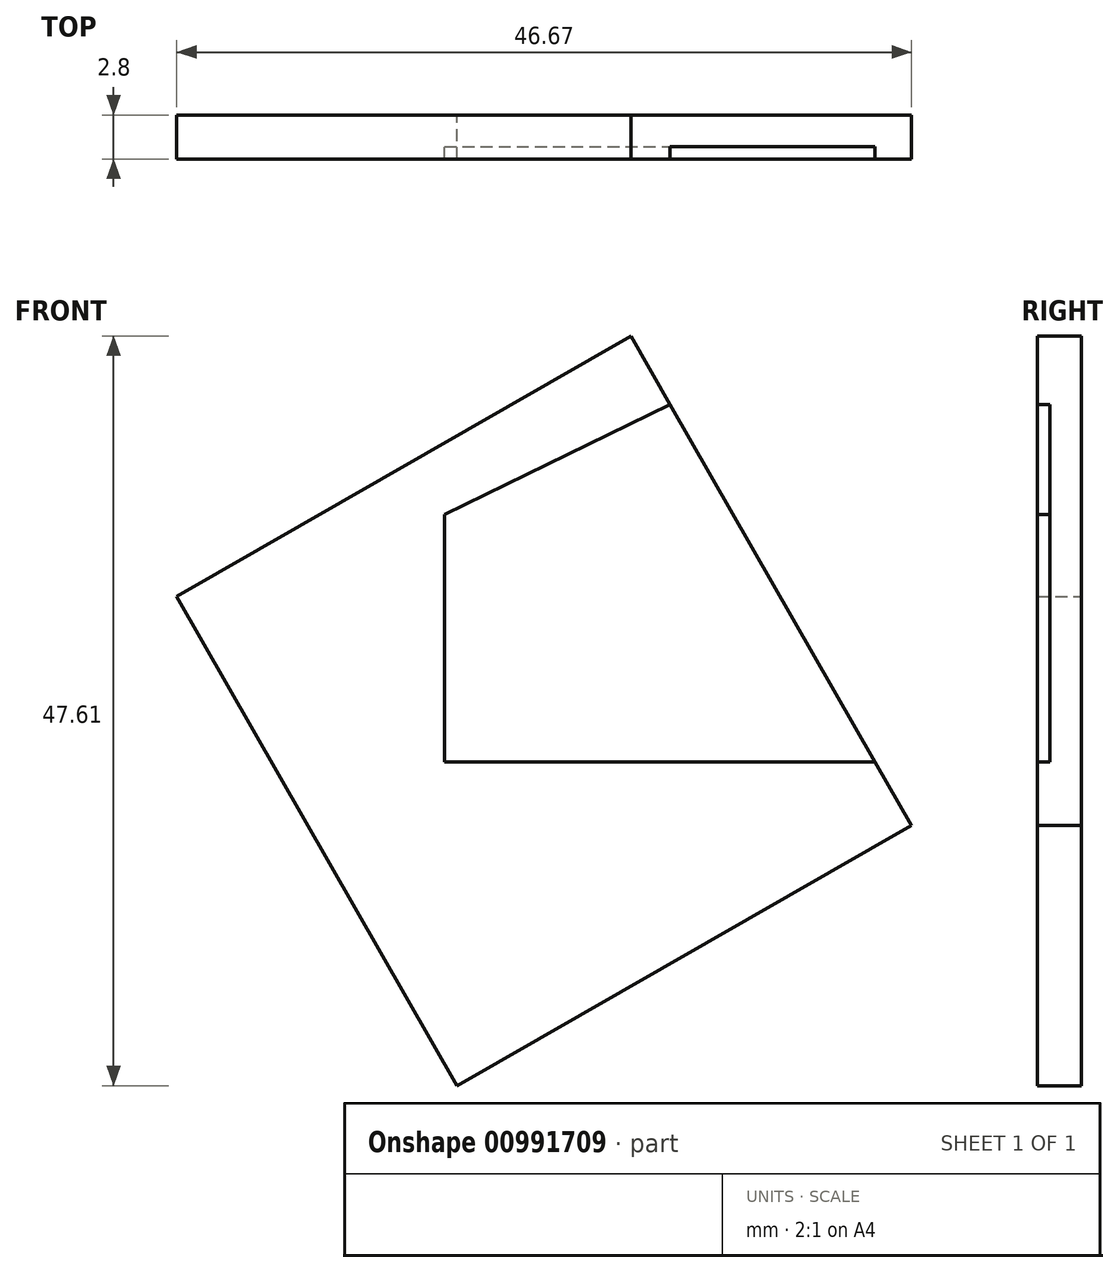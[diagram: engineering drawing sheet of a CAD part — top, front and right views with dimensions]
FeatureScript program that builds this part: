
annotation { "Feature Type Name" : "Feature", "Feature Type Description" : "" }
export const myFeature = defineFeature(function(context is Context, id is Id, definition is map)
    precondition{}
    {
        {
            var Q0;
            Q0=qCreatedBy(makeId("Front.planeOp"),FACE);
            var sketch = newSketch(context, id + "F0", { "sketchPlane" : qUnion([Q0])});
            skLineSegment(sketch, "E0", {"start": v(0, 0) * mm, "end": v(0, 15.7) * mm});
            skLineSegment(sketch, "E1", {"start": v(0, 0) * mm, "end": v(25, 0) * mm});
            skLineSegment(sketch, "E2", {"start": v(16.17, 23.6) * mm, "end": v(0, 15.7) * mm});
            skLineSegment(sketch, "E3", {"start": v(16.17, 23.6) * mm, "end": v(25, 0) * mm});
            skLineSegment(sketch, "E4", {"start": v(16.17, 23.6) * mm, "end": v(20.59, 11.8) * mm});
            skLineSegment(sketch, "E5", {"start": v(20.59, 11.8) * mm, "end": v(0, 0) * mm});
            skLineSegment(sketch, "E6", {"start": v(20.59, 11.8) * mm, "end": v(14.34, 22.7) * mm});
            skLineSegment(sketch, "E7", {"start": v(20.59, 11.8) * mm, "end": v(27.18, 0.3) * mm});
            skLineSegment(sketch, "E8", {"start": v(14.34, 22.7) * mm, "end": v(11.85, 27.04) * mm});
            skLineSegment(sketch, "E9", {"start": v(11.85, 27.04) * mm, "end": v(-17, 10.5) * mm});
            skLineSegment(sketch, "E10", {"start": v(-17, 10.5) * mm, "end": v(-4.69, -10.99) * mm});
            skLineSegment(sketch, "E11", {"start": v(27.18, 0.3) * mm, "end": v(29.66, -4.03) * mm});
            skLineSegment(sketch, "E12", {"start": v(29.66, -4.03) * mm, "end": v(-4.83, -23.8) * mm});
            skLineSegment(sketch, "E13", {"start": v(-4.69, -10.99) * mm, "end": v(0.8, -20.57) * mm});
            skLineSegment(sketch, "E14", {"start": v(25, 0) * mm, "end": v(27.35, 0) * mm});
            skSolve(sketch);
        }
        {
            var Q0;
            {var subQ2=sQuery(id+"F0.wireOp",EDGE,"E0");Q0=makeQuery(id+"F0.imprint","IMPRINT",FACE,{"disambiguationData":[TD([[makeQuery(id+"F0.imprint","IMPRINT",EDGE,{"derivedFrom":subQ2}),1.0]])]});}
            extrude(context, id + "F1", {"entities" : qUnion([Q0]), "depth" : 0.8 * mm, "offsetDistance" : 25 * mm});
        }
        {
            var Q0;
            {var subQ2=sQuery(id+"F0.wireOp",EDGE,"E0");Q0=makeQuery(id+"F0.imprint","IMPRINT",FACE,{"disambiguationData":[TD([[makeQuery(id+"F0.imprint","IMPRINT",EDGE,{"derivedFrom":subQ2}),1.0]])]});}
            var Q1;
            {var subQ0=sQuery(id+"F0.wireOp",EDGE,"E0");Q1=makeQuery(id+"F0.imprint","IMPRINT",FACE,{"disambiguationData":[TD([[makeQuery(id+"F0.imprint","IMPRINT",EDGE,{"derivedFrom":subQ0}),-1.0]])]});}
            var Q2;
            Q2=makeQuery(id+"F0.imprint","IMPRINT",FACE,{"disambiguationData":[TD([[makeQuery(id+"F0.imprint","IMPRINT",EDGE,{"derivedFrom":sQuery(id+"F0.wireOp",EDGE,"E1")}),1.0]])]});
            var Q3;
            Q3=makeQuery(id+"F0.imprint","IMPRINT",FACE,{"disambiguationData":[TD([[makeQuery(id+"F0.imprint","IMPRINT",EDGE,{"derivedFrom":sQuery(id+"F0.wireOp",EDGE,"E3")}),1.0]])]});
            extrude(context, id + "F2", {"entities" : qUnion([Q0, Q1, Q2, Q3]), "operationType" : NewBodyOperationType.ADD, "depth" : -2 * mm, "offsetDistance" : 25 * mm});
        }
    });
